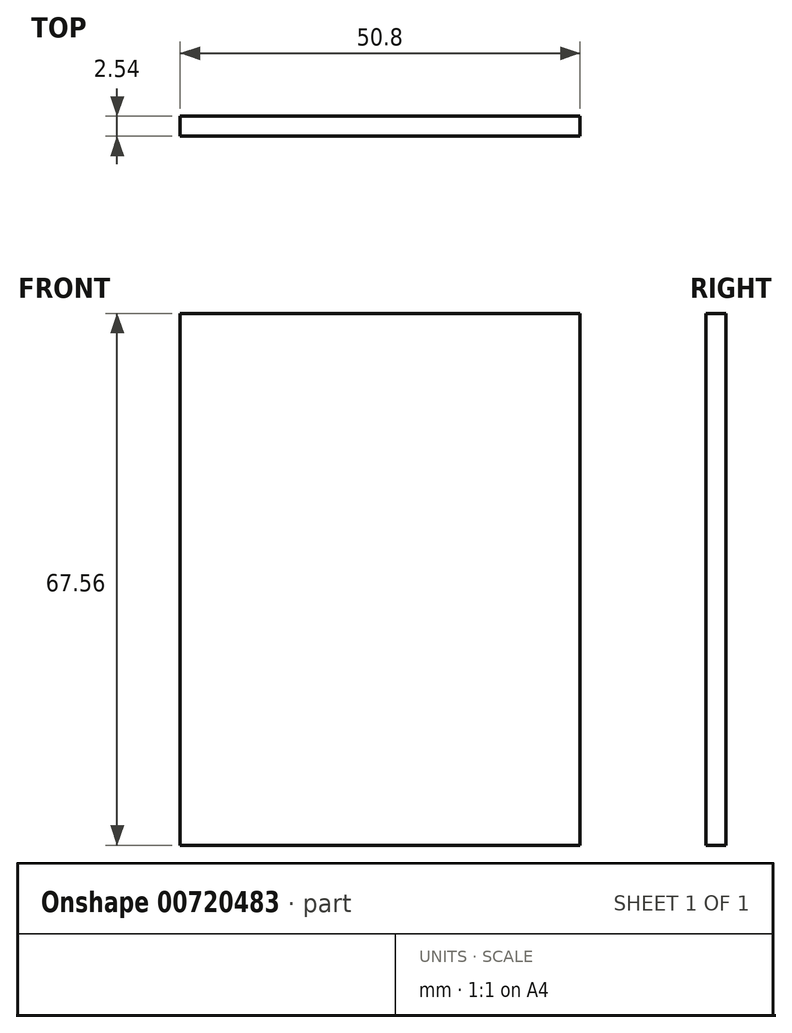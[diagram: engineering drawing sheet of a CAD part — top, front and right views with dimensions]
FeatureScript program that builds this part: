
annotation { "Feature Type Name" : "Feature", "Feature Type Description" : "" }
export const myFeature = defineFeature(function(context is Context, id is Id, definition is map)
    precondition{}
    {
        {
            var Q0;
            Q0=qCreatedBy(makeId("Front.planeOp"),FACE);
            var sketch = newSketch(context, id + "F0", { "sketchPlane" : qUnion([Q0])});
            skLineSegment(sketch, "E0.bottom", {"start": v(-47.49, -0.69) * mm, "end": v(3.31, -0.69) * mm});
            skLineSegment(sketch, "E0.top", {"start": v(-47.49, -68.25) * mm, "end": v(3.31, -68.25) * mm});
            skLineSegment(sketch, "E0.left", {"start": v(-47.49, -0.69) * mm, "end": v(-47.49, -68.25) * mm});
            skLineSegment(sketch, "E0.right", {"start": v(3.31, -0.69) * mm, "end": v(3.31, -68.25) * mm});
            skSolve(sketch);
        }
        {
            var Q0;
            Q0=makeQuery(id+"F0.imprint","IMPRINT",FACE,{"disambiguationData":[TD([[makeQuery(id+"F0.imprint","IMPRINT",EDGE,{"derivedFrom":sQuery(id+"F0.wireOp",EDGE,"E0.bottom")}),-1.0]])]});
            extrude(context, id + "F1", {"entities" : qUnion([Q0]), "depth" : 2.54 * mm, "offsetDistance" : 25.4 * mm});
        }
    });
